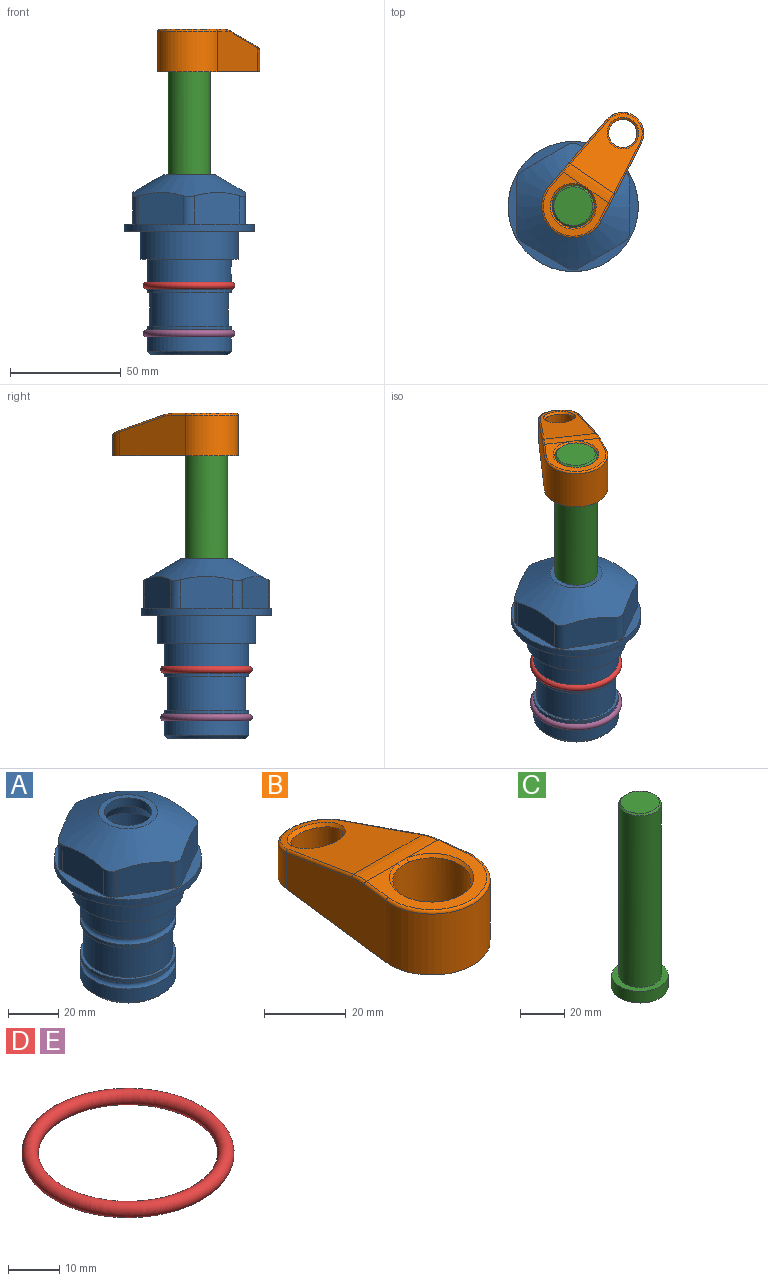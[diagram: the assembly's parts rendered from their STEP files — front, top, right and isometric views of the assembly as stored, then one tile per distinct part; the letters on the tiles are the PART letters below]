
ASSEMBLY  parts=5 mates=4
PART A: 36 faces, bbox 58.7x58.7x81 mm
  f0: cylinder r=17.78mm len=35.56mm, axis (0,0,1), area 1670.8mm2, adj f23,f24,f31
  f1: cylinder r=19.05mm len=38.1mm, axis (0,0,1), area 1191.9mm2, adj f26,f27,f30
  f2: plane 58.66x58.66mm, normal (0,0,-1), area 1150.6mm2, adj f3,f28
  f3: cylinder r=29.33mm len=58.66mm, axis (0,0,-1), area 585.1mm2, adj f2,f4
  f4: plane 58.66x58.66mm, normal (0,0,1), area 475.9mm2, adj f3,f5,f6,f7,f8,f9,f10,f11
  f5: plane 20.32x14.34mm, normal (-0.5,0.87,0), area 324.4mm2, adj f4,f15,f16,f17
  f6: plane 20.32x14.34mm, normal (0.5,0.87,0), area 324.4mm2, adj f4,f14,f15,f17
  f7: plane 23.48x14.34mm, normal (1,0,0), area 324.4mm2, adj f4,f13,f14,f17
  f8: plane 20.32x14.34mm, normal (0.5,-0.87,0), area 324.4mm2, adj f4,f12,f13,f17
  f9: plane 20.32x14.34mm, normal (-0.5,-0.87,0), area 324.4mm2, adj f4,f11,f12,f17
  f10: plane 23.48x14.34mm, normal (-1,0,0), area 324.4mm2, adj f4,f11,f16,f17
  f11: cylinder r=5.08mm len=12.85mm, axis (0,0,-1), area 67.2mm2, adj f4,f9,f10,f17
  f12: cylinder r=5.08mm len=12.85mm, axis (0,0,-1), area 67.2mm2, adj f4,f8,f9,f17
  f13: cylinder r=5.08mm len=12.85mm, axis (0,0,-1), area 67.2mm2, adj f4,f7,f8,f17
  f14: cylinder r=5.08mm len=12.85mm, axis (0,0,-1), area 67.2mm2, adj f4,f6,f7,f17
  f15: cylinder r=5.08mm len=12.85mm, axis (0,0,-1), area 67.2mm2, adj f4,f5,f6,f17
  f16: cylinder r=5.08mm len=12.85mm, axis (0,0,-1), area 67.2mm2, adj f4,f5,f10,f17
  f17: cone r=11.73mm half-angle=60deg, axis (0,0,-1), area 2071.8mm2, adj f5,f6,f7,f8,f9,f10,f11,f12
  f18: plane 23.46x23.46mm, normal (0,0,1), area 147.4mm2, adj f17,f35
  f19: plane 34.93x34.93mm, normal (0,0,-1), area 958mm2, adj f29
  f20: cylinder r=19.05mm len=38.1mm, axis (0,0,1), area 760.1mm2, adj f21,f29
  f21: torus R=19.05mm, axis (0,0,1), area 565.3mm2, adj f20,f22
  f22: cylinder r=19.05mm len=38.1mm, axis (0,0,1), area 190mm2, adj f21,f23
  f23: plane 38.1x38.1mm, normal (0,0,1), area 146.9mm2, adj f0,f22
  f24: plane 38.1x38.1mm, normal (0,0,-1), area 146.9mm2, adj f0,f25
  f25: cylinder r=19.05mm len=38.1mm, axis (0,0,1), area 190mm2, adj f24,f26
  f26: torus R=19.05mm, axis (0,0,1), area 565.3mm2, adj f1,f25
  f27: plane 44.45x44.45mm, normal (0,0,-1), area 411.7mm2, adj f1,f28
  f28: cylinder r=22.23mm len=44.45mm, axis (0,0,1), area 1773.5mm2, adj f2,f27
  f29: cone r=19.05mm half-angle=45deg, axis (0,0,1), area 257.5mm2, adj f19,f20
  f30: cylinder r=3.17mm len=6.75mm, axis (-1,0,0), area 128mm2, adj f1,f33
  f31: cylinder r=3.17mm len=6.35mm, axis (-1,0,0), area 102.5mm2, adj f0,f33
  f32: plane 25.4x25.4mm, normal (0,0,1), area 506.7mm2, adj f33
  f33: cylinder r=12.7mm len=66.42mm, axis (0,0,-1), area 5236.2mm2, adj f30,f31,f32,f34
  f34: cone r=9.53mm half-angle=30deg, axis (0,0,-1), area 443.4mm2, adj f33,f35
  f35: cylinder r=9.53mm len=19.05mm, axis (0,0,-1), area 240.9mm2, adj f18,f34
PART B: 31 faces, bbox 31.7x65.5x19.8 mm
  f0: plane 39.12x18.26mm, normal (0.99,0.12,0), area 612.2mm2, adj f1,f4,f7,f11,f13,f15
  f1: cylinder r=9.53mm len=18.91mm, axis (0,0,-1), area 296.1mm2, adj f0,f2,f7,f17
  f2: plane 39.12x18.26mm, normal (-0.99,0.12,0), area 612.2mm2, adj f1,f4,f7,f12,f14,f16
  f3: cylinder r=6.35mm len=12.7mm, axis (0,0,-1), area 362.4mm2, adj f7,f18
  f4: cylinder r=14.29mm len=28.58mm, axis (0,0,-1), area 882.2mm2, adj f0,f2,f7,f10
  f5: cylinder r=9.53mm len=19.05mm, axis (0,0,-1), area 1092.6mm2, adj f7,f19,f20
  f6: plane 26.99x23.69mm, normal (0,0,1), area 216.2mm2, adj f9,f10,f11,f12,f19
  f7: plane 63.5x28.58mm, normal (0,0,-1), area 661.8mm2, adj f0,f1,f2,f3,f4,f5,f22,f23
  f8: plane 33.52x23.6mm, normal (0,0.26,0.97), area 486mm2, adj f9,f15,f16,f17,f18
  f9: cylinder r=19.05mm len=24.72mm, axis (1,0,0), area 120.4mm2, adj f6,f8,f13,f14,f20
  f10: torus R=13.49mm, axis (0,0,1), area 59mm2, adj f4,f6,f11,f12
  f11: cylinder r=0.79mm len=8.67mm, axis (0.12,-0.99,0), area 10.8mm2, adj f0,f6,f10,f13
  f12: cylinder r=0.79mm len=8.67mm, axis (0.12,0.99,0), area 10.8mm2, adj f2,f6,f10,f14
  f13: bspline ~4.95x1.42mm, area 6.1mm2, adj f0,f9,f11,f15
  f14: bspline ~4.95x1.42mm, area 6.1mm2, adj f2,f9,f12,f16
  f15: cylinder r=0.79mm len=25.95mm, axis (0.12,-0.96,0.26), area 32.9mm2, adj f0,f8,f13,f17
  f16: cylinder r=0.79mm len=25.95mm, axis (0.12,0.96,-0.26), area 32.9mm2, adj f2,f8,f14,f17
  f17: bspline ~18.91x8.38mm, area 30mm2, adj f1,f8,f15,f16
  f18: bspline ~14.29x14.29mm, area 48.3mm2, adj f3,f8
  f19: cone r=9.53mm half-angle=45deg, axis (0,0,1), area 66.5mm2, adj f5,f6,f20
  f20: bspline ~3.22x0.96mm, area 3.5mm2, adj f5,f9,f19
  f21: plane 2.75x2.72mm, normal (0,0,-1), area 2.9mm2, adj f23,f25,f28
  f22: plane 23.05x15.88mm, normal (-0.99,-0.12,0), area 323.6mm2, adj f7,f25,f26,f27,f28,f29
  f23: plane 23.05x15.88mm, normal (0.99,-0.12,0), area 323.6mm2, adj f7,f21,f25,f27,f28,f30
  f24: cylinder r=9.53mm len=10.69mm, axis (0,0,-1), area 114.7mm2, adj f7,f27,f29,f30
  f25: cylinder r=12.7mm len=20.59mm, axis (0,0,-1), area 381.1mm2, adj f7,f21,f22,f23,f26,f28
  f26: plane 2.75x2.72mm, normal (0,0,-1), area 2.9mm2, adj f22,f25,f28
  f27: plane 19.72x18.37mm, normal (0,-0.26,-0.97), area 291.8mm2, adj f22,f23,f24,f28,f29,f30
  f28: cylinder r=15.88mm len=19.92mm, axis (1,0,0), area 54.8mm2, adj f21,f22,f23,f25,f26,f27
  f29: cylinder r=1.59mm len=11mm, axis (0,0,-1), area 34.7mm2, adj f7,f22,f24,f27
  f30: cylinder r=1.59mm len=11mm, axis (0,0,-1), area 34.7mm2, adj f7,f23,f24,f27
PART C: 6 faces, bbox 25.4x25.4x101.6 mm
  f0: plane 17.46x17.46mm, normal (0,0,1), area 239.5mm2, adj f5
  f1: plane 25.4x25.4mm, normal (0,0,-1), area 506.7mm2, adj f2
  f2: cylinder r=12.7mm len=25.4mm, axis (0,0,1), area 506.7mm2, adj f1,f3
  f3: plane 25.4x25.4mm, normal (0,0,1), area 221.7mm2, adj f2,f4
  f4: cylinder r=9.53mm len=94.46mm, axis (0,0,1), area 5653mm2, adj f3,f5
  f5: cone r=8.73mm half-angle=45deg, axis (0,0,-1), area 64.4mm2, adj f0,f4
PART D: 1 faces, bbox 44.7x44.7x3.2 mm
  f0: torus R=19.05mm, axis (0,0,1), area 1193.9mm2
PART E: same geometry as D
PLACE A at identity fixed
PLACE B rot(axis=(0,0,-1),34.2deg) t=(0,0,27.55)mm
PLACE C rot(axis=(0,0,-1),34.2deg) t=(0,0,27.55)mm
PLACE D at identity
PLACE E t=(0,0,-21.59)mm
MATE cylindrical A.f0 <-> C.f2  axis (0,0,1) through (0,0,-50.55)mm
MATE fastened E.f0 <-> A.f0  axis (0,0,1) through (0,0,-46.1)mm
MATE fastened B.f4 <-> C.f2  axis (0,0,1) through (0,0,91.05)mm
MATE fastened D.f0 <-> A.f0  axis (0,0,1) through (0,0,-24.51)mm
